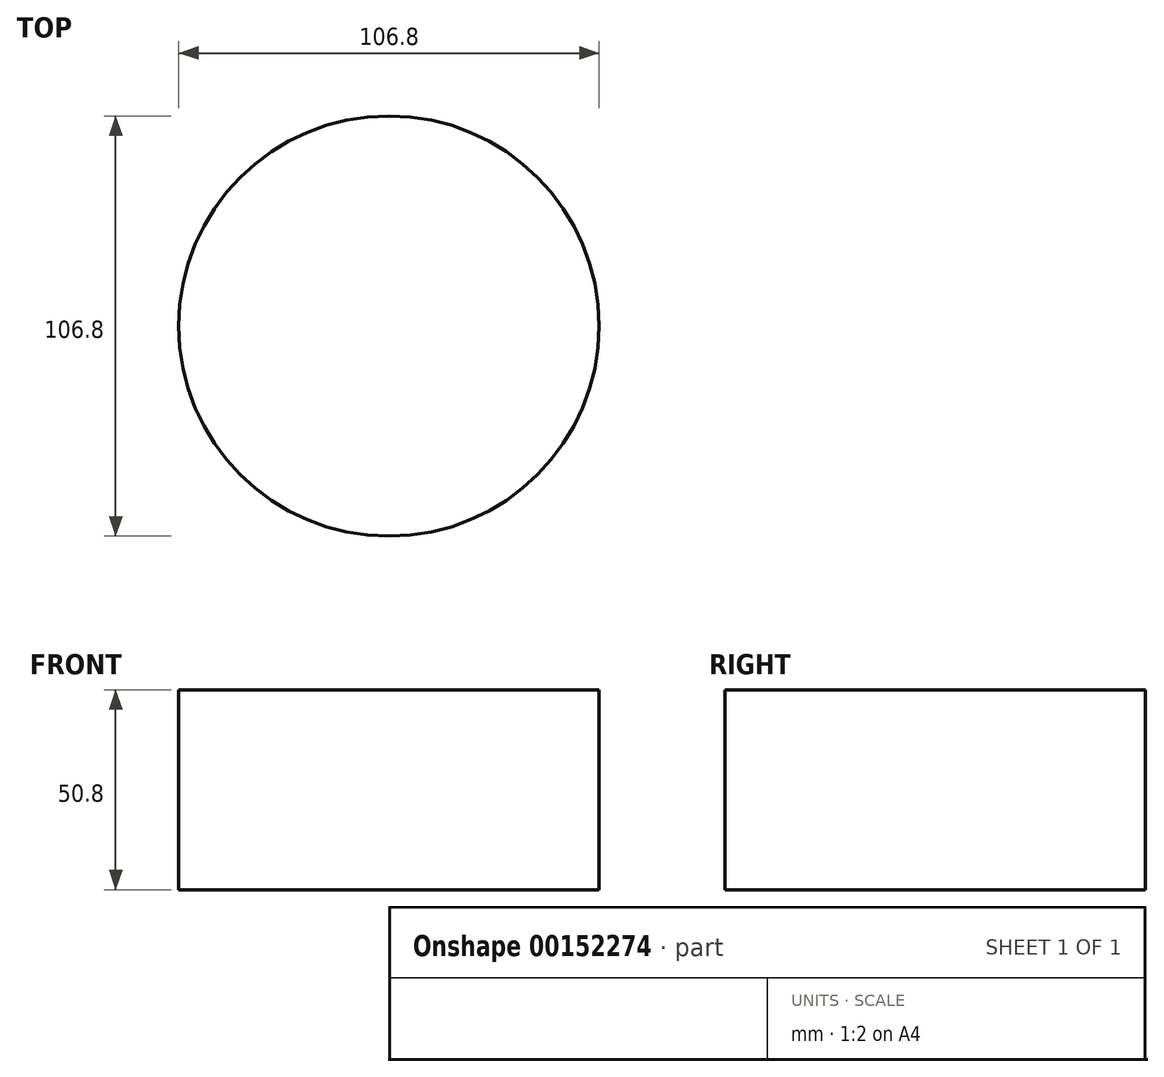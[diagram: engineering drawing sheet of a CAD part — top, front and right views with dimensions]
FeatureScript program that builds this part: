
annotation { "Feature Type Name" : "Feature", "Feature Type Description" : "" }
export const myFeature = defineFeature(function(context is Context, id is Id, definition is map)
    precondition{}
    {
        {
            var Q0;
            Q0=qCreatedBy(makeId("Top.planeOp"),FACE);
            var sketch = newSketch(context, id + "F0", { "sketchPlane" : qUnion([Q0])});
            skCircle(sketch, "E0", {"center": v(0, 0) * mm, "radius": 53.4 * mm});
            skSolve(sketch);
        }
        {
            var Q0;
            Q0 = qSketchRegion(id + "F0", true);
            extrude(context, id + "F1", {"entities" : qUnion([Q0]), "depth" : 50.8 * mm});
        }
    });
